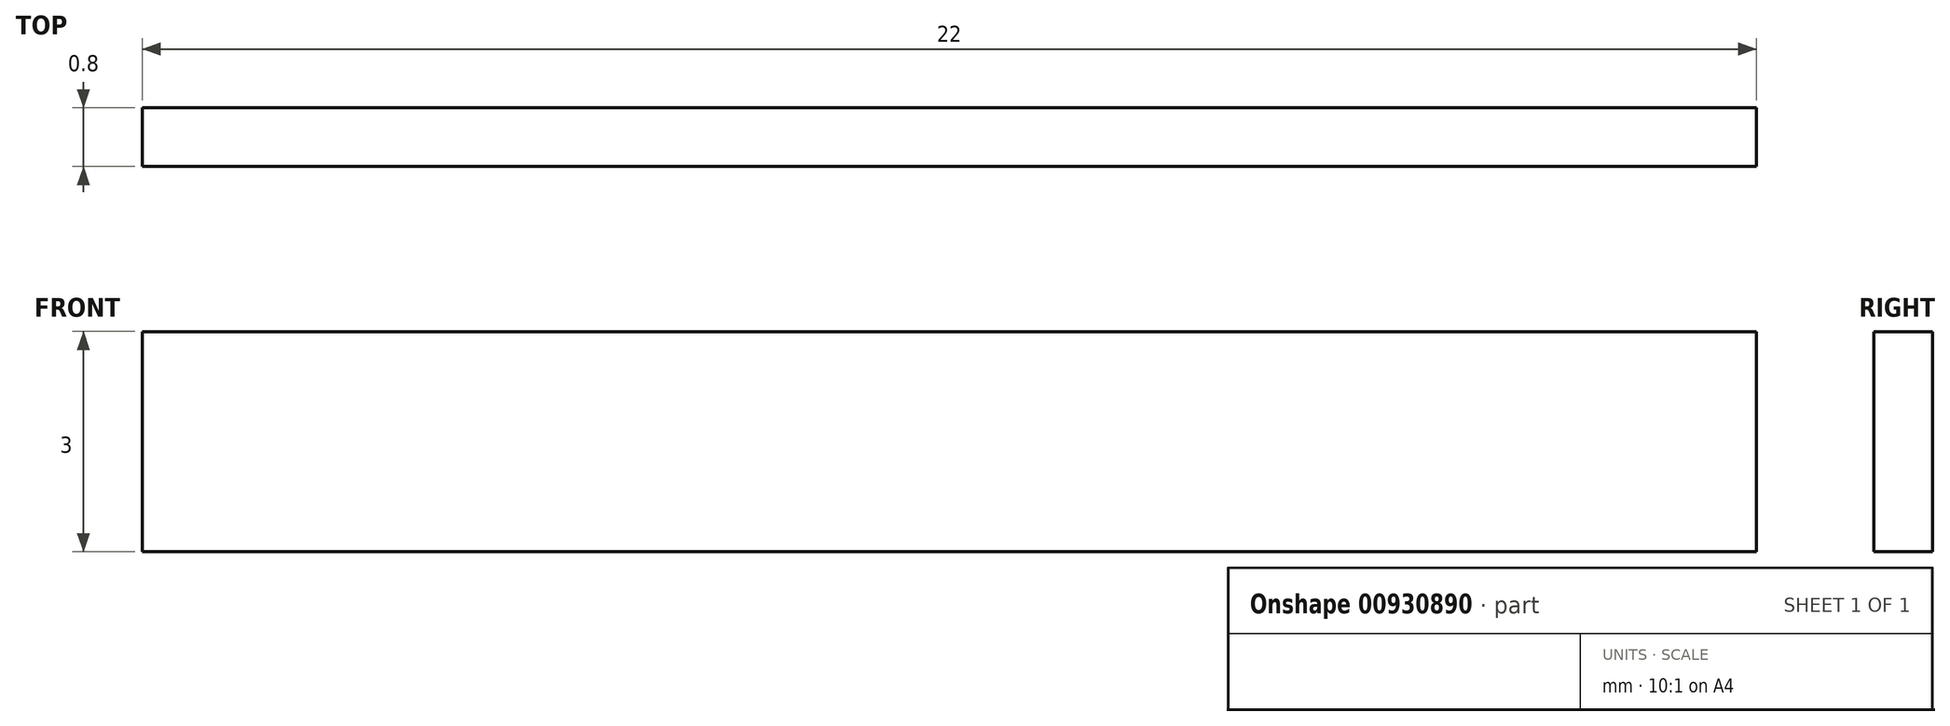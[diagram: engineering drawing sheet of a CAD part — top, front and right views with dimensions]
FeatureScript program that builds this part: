
annotation { "Feature Type Name" : "Feature", "Feature Type Description" : "" }
export const myFeature = defineFeature(function(context is Context, id is Id, definition is map)
    precondition{}
    {
        {
            var Q0;
            Q0=qCreatedBy(makeId("Front.planeOp"),FACE);
            var sketch = newSketch(context, id + "F0", { "sketchPlane" : qUnion([Q0])});
            skLineSegment(sketch, "E0.bottom", {"start": v(11, 2.18) * mm, "end": v(-11, 2.18) * mm});
            skLineSegment(sketch, "E0.top", {"start": v(11, -0.82) * mm, "end": v(-11, -0.82) * mm});
            skLineSegment(sketch, "E0.left", {"start": v(11, 2.18) * mm, "end": v(11, -0.82) * mm});
            skLineSegment(sketch, "E0.right", {"start": v(-11, 2.18) * mm, "end": v(-11, -0.82) * mm});
            skPoint(sketch, "E0.middle", {"position": v(0, 0.68) * mm});
            skSolve(sketch);
        }
        {
            var Q0;
            Q0=makeQuery(id+"F0.imprint","IMPRINT",FACE,{"disambiguationData":[TD([[makeQuery(id+"F0.imprint","IMPRINT",EDGE,{"derivedFrom":sQuery(id+"F0.wireOp",EDGE,"E0.bottom")}),1.0]])]});
            extrude(context, id + "F1", {"entities" : qUnion([Q0]), "depth" : .80 * mm, "offsetDistance" : 25 * mm});
        }
    });
